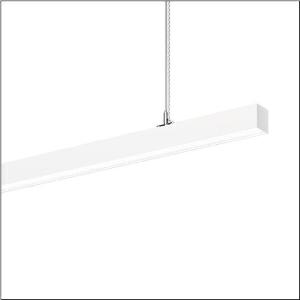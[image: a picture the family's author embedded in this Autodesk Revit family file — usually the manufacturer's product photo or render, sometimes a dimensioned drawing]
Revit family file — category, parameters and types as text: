
# Revit family: silica_r__21_51mx33dc4dwb_294c
name_source: partatom
category: Lighting Fixtures
units: mm (PartAtom-declared; Revit-internal decimal feet)

## family parameters
Cut with Voids When Loaded = No
Host = Face
Light Source = No
Part Type = Normal
Room Calculation Point = No
Round Connector Dimension = Use Diameter
Shared = No

## types (1)
- --- (1 x LED, 14790 lm, 93.9 W, 4000K)
    Apparent Load = 94 VA
    CIE Flux Codes = 78 96 99 55 100
    Color Rendering = 80
    Color Temperature = 4000K
    Default Elevation = 1800 mm
    Description = Silica® 21, office luminaire, primary optical cover: prismatic diffuser, of PMMA, CAT 2 (L<= 3000cd/m²), light emission: direct/indirect distribution, primary light characteristic: symmetric, installation type: suspended mounting, LED, rated luminous flux: 14.790lm, luminous efficacy: 158lm/W, light colour: 840, colour temperature: 4000K, with terminal, 3+2-pole, max. 2.5mm², mains connection: 220..240V, AC, 50/60Hz, rated input power: 93.9W, luminaire housing, of aluminium, traffic white (RAL 9016), length: 3.004mm, width: 53mm, height: 53mm, protection rating (complete): IP20, insulation class (complete): insulation class I (protective earthing), certification: CE, permissible operating ambient temperature: 0..+35°C, standard: EN 50419, packaging unit: 1 piece
    Height = 53 mm
    Lamp = 1 x LED
    Lamp Light Flux = 14790 lm
    Lamp Power = 93.9 W
    Lamp count = 1
    Length = 3004 mm
    Luminous efficacy = 158 lm/W
    Manufacturer = Siteco
    ModVariant = No
    Model = 51MX33DC4DWB
    Mounting Place = Ceiling
    Mounting Type = Pendant
    Number of Poles = 1
    OnlyDefault = Yes
    Power Factor = 1
    Product Name = Silica® 21
    Product group = office luminaire | ceiling pendant
    ProductGroupID = 902
    Protection Class = Protection class I
    Protection Degree = IP 20
    RLX_Detail_Level = 1
    RLX_Emergency_Light_Flux = 0 lm
    RLX_Emergency_Type = 0
    RLX_Emergency_Type_DB = No
    RlxData = <blob elided: 21433 chars, md5=bac81aaf>
    Socket = socket
    Standby Power = 0 W
    System Light Flux = 14790 lm
    System Power = 94 W
    Type Comments = factory setting: luminous flux: 100 % | dim-lin: 254 | 323 mA
    Type Image = l_1297784.jpg
    URL = http://relux.com
    VarID = @adj_049195
    Voltage = 0 V
    Weight = 0.00 kg
    Width = 53 mm

## geometry (parser evidence)
native form markers: Blend x4, Sweep x15
no freeform markers — native parametric forms only
